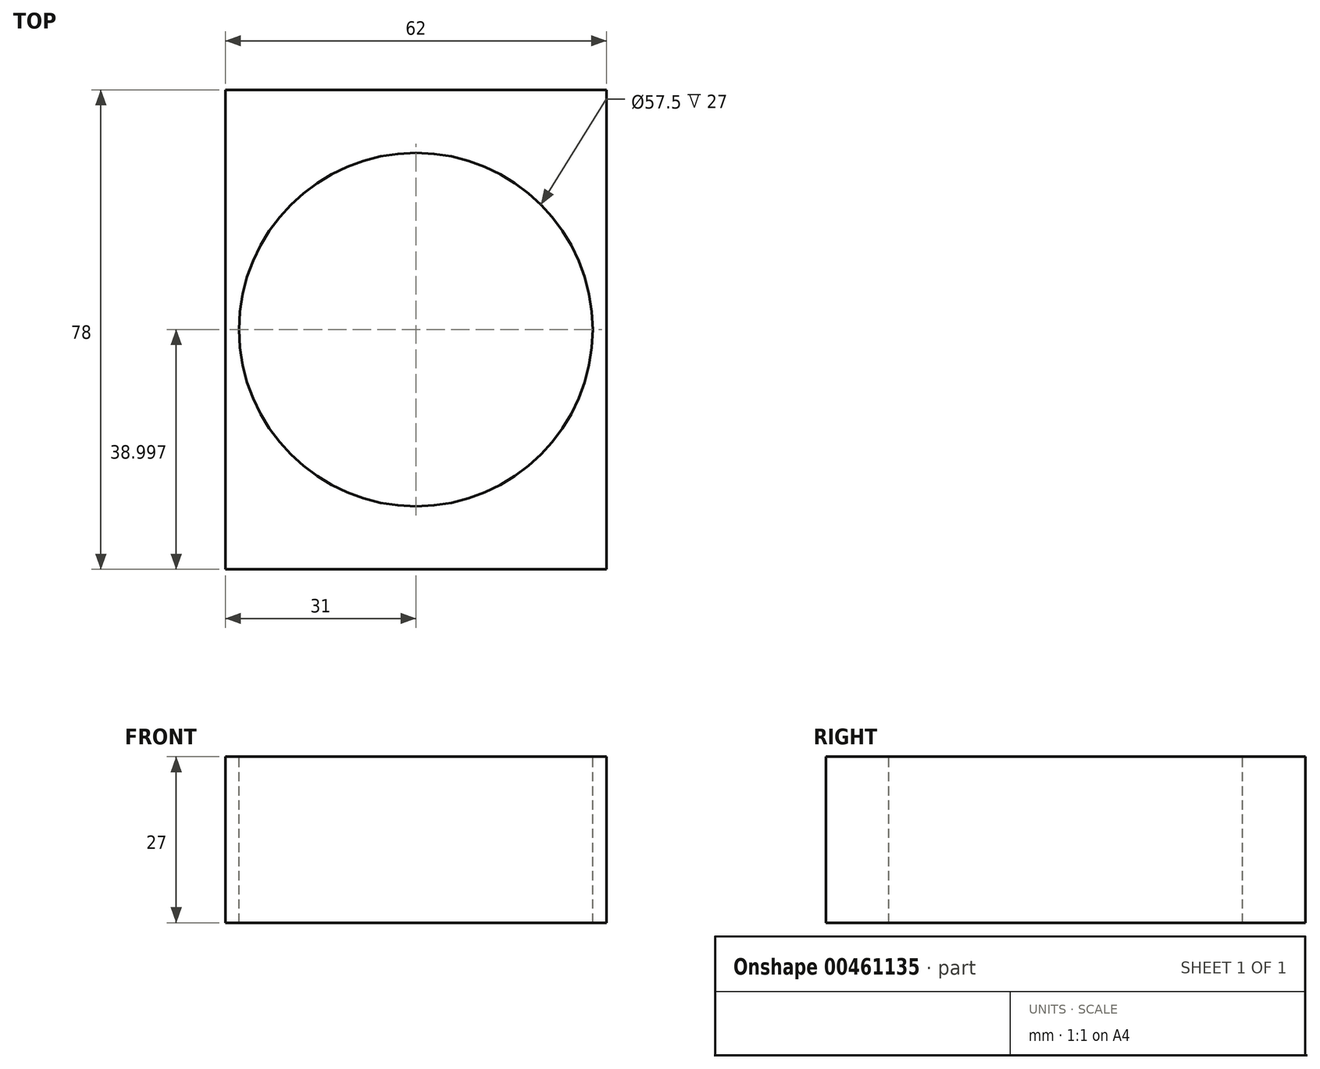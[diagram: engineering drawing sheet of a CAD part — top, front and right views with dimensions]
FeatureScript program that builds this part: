
annotation { "Feature Type Name" : "Feature", "Feature Type Description" : "" }
export const myFeature = defineFeature(function(context is Context, id is Id, definition is map)
    precondition{}
    {
        {
            var Q0;
            Q0=qCreatedBy(makeId("Top.planeOp"),FACE);
            var sketch = newSketch(context, id + "F0", { "sketchPlane" : qUnion([Q0])});
            skLineSegment(sketch, "E0.bottom", {"start": v(-26.4, 55.84) * mm, "end": v(35.6, 55.84) * mm});
            skLineSegment(sketch, "E0.top", {"start": v(-26.4, -22.16) * mm, "end": v(35.6, -22.16) * mm});
            skLineSegment(sketch, "E0.left", {"start": v(-26.4, 55.84) * mm, "end": v(-26.4, -22.16) * mm});
            skLineSegment(sketch, "E0.right", {"start": v(35.6, 55.84) * mm, "end": v(35.6, -22.16) * mm});
            skLineSegment(sketch, "E1", {"start": v(-26.4, -22.16) * mm, "end": v(35.6, 55.84) * mm, "construction": true});
            skSolve(sketch);
        }
        {
            var Q0;
            Q0 = qSketchRegion(id + "F0", true);
            extrude(context, id + "F1", {"entities" : qUnion([Q0]), "depth" : 27 * mm});
        }
        {
            var Q0;
            Q0=makeQuery(id+"F1.opExtrude","CAP_FACE",FACE,{"disambiguationData":[OSD([sQuery(id+"F0.wireOp",EDGE,"E0.bottom"),sQuery(id+"F0.wireOp",EDGE,"E0.top"),sQuery(id+"F0.wireOp",EDGE,"E0.left"),sQuery(id+"F0.wireOp",EDGE,"E0.right")])],"isStart":false});
            var sketch = newSketch(context, id + "F2", { "sketchPlane" : qUnion([Q0])});
            skCircle(sketch, "E2", {"center": v(4.6, 16.84) * mm, "radius": 28.75 * mm});
            skSolve(sketch);
        }
        {
            var Q0;
            Q0 = qSketchRegion(id + "F2", true);
            extrude(context, id + "F3", {"entities" : qUnion([Q0]), "operationType" : NewBodyOperationType.REMOVE, "oppositeDirection" : true, "depth" : 27 * mm});
        }
    });
